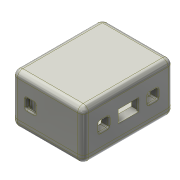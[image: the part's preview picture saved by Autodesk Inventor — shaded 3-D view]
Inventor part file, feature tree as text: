
AUTODESK INVENTOR PART (.ipt)
format: ipt  version: 2021 (Build 250183000, 183)  size: 764,928 bytes
history: native  units: mm
features: sketch x17, projected_geometry x17, extrude x14, other x5, fillet x5, hole x3, shell x1, mirror x1
ambient origin geometry x8: Origin, YZ Plane, XZ Plane, XY Plane, X Axis, Y Axis, Z Axis, Center Point
bodies: Body1 (feature_tree), Body2 (feature_tree)
feature tree (63):
  other  "Твердое тело1"
  extrude  "Выдавливание1"  Depth=40.0mm
  shell  "Оболочка1"  Thickness=60.0mm
  extrude  "Выдавливание15"  Depth=30.0mm TaperAngle=0.0deg
  extrude  "Выдавливание16"  Depth=3.0mm
  fillet  "Сопряжение1"  Radius=4.0mm
  other  "РабПлоскость1"
  other  "Разделение1"
  extrude  "Выдавливание17"  [1 undecoded]
  fillet  "Сопряжение2"  Radius=2.0mm
  hole  "Отверстие5"  [1 undecoded]
  extrude  "Выдавливание18"  Depth=3.0mm TaperAngle=0.0deg
  fillet  "Сопряжение3"  Radius=3.0mm
  extrude  "Выдавливание20"  TaperAngle=45.0deg  [1 undecoded]
  extrude  "Выдавливание21"  Depth=3.7mm
  extrude  "Выдавливание22"  Depth=2.5mm
  extrude  "Выдавливание23"  Depth=46.0mm
  extrude  "Выдавливание25"  Depth=60.0mm
  extrude  "Выдавливание26"  Depth=20.0mm
  hole  "Отверстие6"  [1 undecoded]
  extrude  "Выдавливание27"  Depth=41.0mm
  fillet  "Сопряжение6"  [1 undecoded]
  extrude  "Выдавливание30"  Depth=3.0mm TaperAngle=0.0deg
  mirror  "Зеркальное отражение1"
  hole  "Отверстие7"  [1 undecoded]
  extrude  "Выдавливание31"  Depth=14.8mm
  fillet  "Сопряжение7"  Radius=1.1mm
  sketch  "Эскиз1"
  sketch  "Эскиз22"
  projected_geometry  "Спроецированная петля18"
  sketch  "Эскиз23"
  projected_geometry  "Спроецированная петля19"
  projected_geometry  "Спроецированная петля20"
  projected_geometry  "Спроецированная петля21"
  sketch  "Эскиз24"
  projected_geometry  "Спроецированная петля22"
  sketch  "Эскиз25"
  projected_geometry  "Спроецированная петля23"
  sketch  "Эскиз26"
  projected_geometry  "Спроецированная петля24"
  sketch  "Эскиз28"
  projected_geometry  "Спроецированная петля26"
  sketch  "Эскиз29"
  projected_geometry  "Спроецированная петля27"
  sketch  "Эскиз30"
  projected_geometry  "Спроецированная петля28"
  sketch  "Эскиз31"
  sketch  "Эскиз33"
  projected_geometry  "Спроецированная петля30"
  sketch  "Эскиз34"
  sketch  "Эскиз35"
  projected_geometry  "Спроецированная петля32"
  sketch  "Эскиз36"
  projected_geometry  "Спроецированная петля33"
  sketch  "Эскиз39"
  projected_geometry  "Спроецированная петля39"
  sketch  "Эскиз40"
  projected_geometry  "Спроецированная петля40"
  projected_geometry  "Спроецированная петля41"
  sketch  "Эскиз41"
  projected_geometry  "Спроецированная петля42"
  other  "Твердое тело2"
  other  "Твердое тело3"
note: 6 required parameter values undecoded (feature->parameter linkage not recoverable at this tier; creation-order binding heuristic only, values carry confidence <= 0.55)
